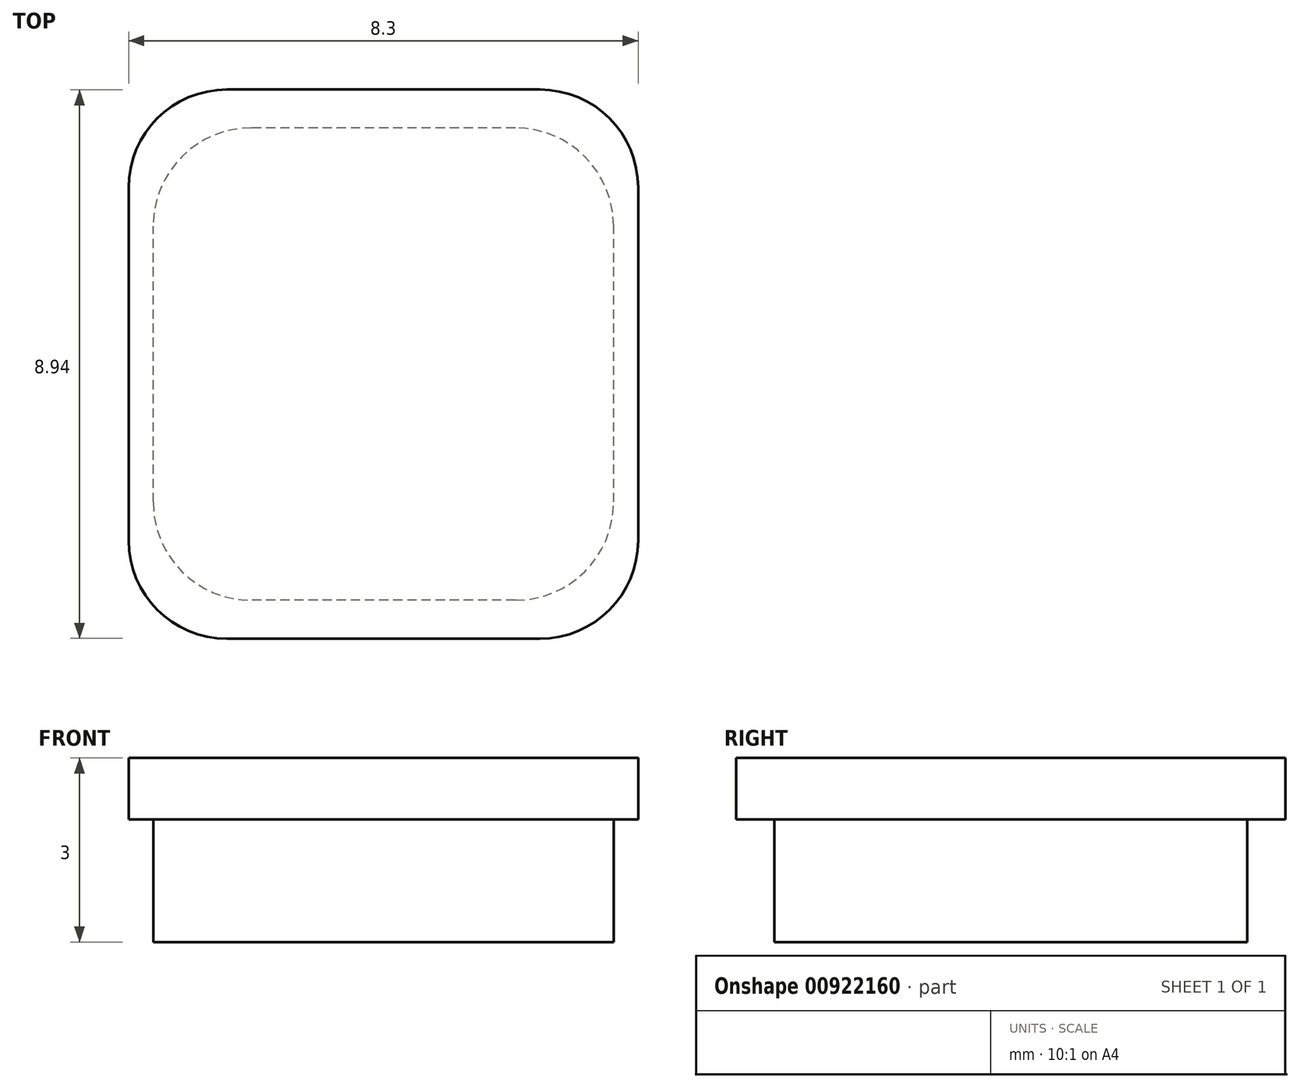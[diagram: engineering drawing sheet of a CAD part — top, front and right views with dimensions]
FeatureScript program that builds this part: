
annotation { "Feature Type Name" : "Feature", "Feature Type Description" : "" }
export const myFeature = defineFeature(function(context is Context, id is Id, definition is map)
    precondition{}
    {
        {
            var Q0;
            Q0=qCreatedBy(makeId("Top.planeOp"),FACE);
            var sketch = newSketch(context, id + "F0", { "sketchPlane" : qUnion([Q0])});
            skLineSegment(sketch, "E0.bottom", {"start": v(3.75, -3.85) * mm, "end": v(-3.75, -3.85) * mm});
            skLineSegment(sketch, "E0.top", {"start": v(3.75, 3.85) * mm, "end": v(-3.75, 3.85) * mm});
            skLineSegment(sketch, "E0.left", {"start": v(3.75, -3.85) * mm, "end": v(3.75, 3.85) * mm});
            skLineSegment(sketch, "E0.right", {"start": v(-3.75, -3.85) * mm, "end": v(-3.75, 3.85) * mm});
            skPoint(sketch, "E0.middle", {"position": v(0, 0) * mm});
            skLineSegment(sketch, "E1.bottom", {"start": v(4.15, -4.47) * mm, "end": v(-4.15, -4.48) * mm});
            skLineSegment(sketch, "E1.top", {"start": v(4.15, 4.48) * mm, "end": v(-4.15, 4.47) * mm});
            skLineSegment(sketch, "E1.left", {"start": v(4.15, -4.47) * mm, "end": v(4.15, 4.48) * mm});
            skLineSegment(sketch, "E1.right", {"start": v(-4.15, -4.48) * mm, "end": v(-4.15, 4.47) * mm});
            skSolve(sketch);
        }
        {
            var Q0;
            Q0=makeQuery(id+"F0.imprint","IMPRINT",FACE,{"disambiguationData":[TD([[makeQuery(id+"F0.imprint","IMPRINT",EDGE,{"derivedFrom":sQuery(id+"F0.wireOp",EDGE,"E0.bottom")}),1.0]])]});
            var Q1;
            Q1=makeQuery(id+"F0.imprint","IMPRINT",FACE,{"disambiguationData":[TD([[makeQuery(id+"F0.imprint","IMPRINT",EDGE,{"derivedFrom":sQuery(id+"F0.wireOp",EDGE,"E0.bottom")}),-1.0]])]});
            extrude(context, id + "F1", {"entities" : qUnion([Q0, Q1]), "depth" : 1 * mm, "offsetDistance" : 25 * mm});
        }
        {
            var Q0;
            Q0=makeQuery(id+"F0.imprint","IMPRINT",FACE,{"disambiguationData":[TD([[makeQuery(id+"F0.imprint","IMPRINT",EDGE,{"derivedFrom":sQuery(id+"F0.wireOp",EDGE,"E0.bottom")}),-1.0]])]});
            extrude(context, id + "F2", {"entities" : qUnion([Q0]), "operationType" : NewBodyOperationType.ADD, "oppositeDirection" : true, "depth" : 2 * mm, "offsetDistance" : 25 * mm});
        }
        {
            var Q0;
            Q0=makeQuery(id+"F1.opExtrude","SWEPT_EDGE",EDGE,{"disambiguationData":[OSD([sQuery(id+"F0.wireOp",EDGE,"E1.top"),sQuery(id+"F0.wireOp",EDGE,"E1.right")])]});
            var Q1;
            Q1=makeQuery(id+"F1.opExtrude","SWEPT_EDGE",EDGE,{"disambiguationData":[OSD([sQuery(id+"F0.wireOp",EDGE,"E1.bottom"),sQuery(id+"F0.wireOp",EDGE,"E1.right")])]});
            var Q2;
            Q2=makeQuery(id+"F1.opExtrude","SWEPT_EDGE",EDGE,{"disambiguationData":[OSD([sQuery(id+"F0.wireOp",EDGE,"E1.top"),sQuery(id+"F0.wireOp",EDGE,"E1.left")])]});
            var Q3;
            Q3=makeQuery(id+"F1.opExtrude","SWEPT_EDGE",EDGE,{"disambiguationData":[OSD([sQuery(id+"F0.wireOp",EDGE,"E1.bottom"),sQuery(id+"F0.wireOp",EDGE,"E1.left")])]});
            var Q4;
            Q4=makeQuery(id+"F2.opExtrude","SWEPT_EDGE",EDGE,{"disambiguationData":[OSD([sQuery(id+"F0.wireOp",EDGE,"E0.bottom"),sQuery(id+"F0.wireOp",EDGE,"E0.left")])]});
            var Q5;
            Q5=makeQuery(id+"F2.opExtrude","SWEPT_EDGE",EDGE,{"disambiguationData":[OSD([sQuery(id+"F0.wireOp",EDGE,"E0.top"),sQuery(id+"F0.wireOp",EDGE,"E0.left")])]});
            var Q6;
            Q6=makeQuery(id+"F2.opExtrude","SWEPT_EDGE",EDGE,{"disambiguationData":[OSD([sQuery(id+"F0.wireOp",EDGE,"E0.bottom"),sQuery(id+"F0.wireOp",EDGE,"E0.right")])]});
            var Q7;
            Q7=makeQuery(id+"F2.opExtrude","SWEPT_EDGE",EDGE,{"disambiguationData":[OSD([sQuery(id+"F0.wireOp",EDGE,"E0.top"),sQuery(id+"F0.wireOp",EDGE,"E0.right")])]});
            fillet(context, id + "F3", {"entities" : qUnion([Q0, Q1, Q2, Q3, Q4, Q5, Q6, Q7]), "radius" : 1.6 * mm, "tangentPropagation" : true, "allowEdgeOverflow" : false});
        }
    });
